# Revit family: REC-01_RFA
name_source: partatom
category: Plumbing Fixtures
units: mm (PartAtom-declared; Revit-internal decimal feet)

## family parameters
Always vertical = Yes
Cut with Voids When Loaded = No
OmniClass Number = 23.45.00.00
OmniClass Title = Sanitary, Laundry, and Cleaning Equipment
Part Type = Normal
Room Calculation Point = No
Round Connector Dimension = Use Diameter
Shared = No
Work Plane-Based = No

## types (1)
- REC-01
    Brass Chromed = Brass
    Compliance = NOM-008-CONAGUA-1998
    Default Elevation = 0"
    Description = Fixed Stream Shower Head
    Features = Medium And High Pressure Shower Head With Anticalcareous
    Inlet Threads = ½" - 14 NPT
    Manufacturer = HELVEX
    Max. Working Pressure = 85.3 psi
    Min. Working Pressure = 14.2 psi
    Model = REC-01
    Support Base Diameter = 2"
    Total Diameter = 5"
    Total Height = 7"
    Total Length = 10"
    Type Comments = Shower Head

## geometry (parser evidence)
native form markers: Sweep x3
no freeform markers — native parametric forms only
